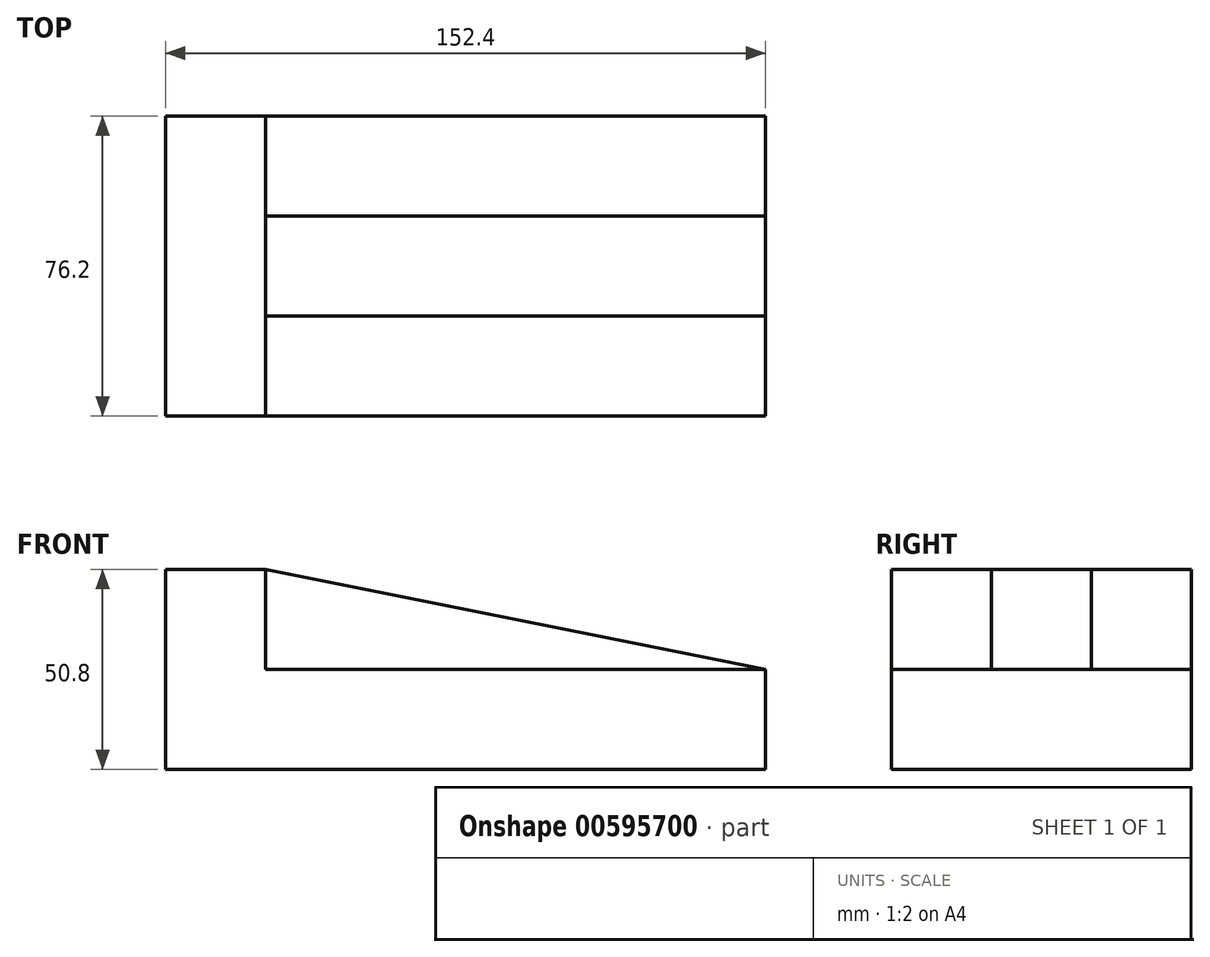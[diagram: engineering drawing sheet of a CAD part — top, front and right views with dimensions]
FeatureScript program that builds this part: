
annotation { "Feature Type Name" : "Feature", "Feature Type Description" : "" }
export const myFeature = defineFeature(function(context is Context, id is Id, definition is map)
    precondition{}
    {
        {
            var Q0;
            Q0=qCreatedBy(makeId("Top.planeOp"),FACE);
            var sketch = newSketch(context, id + "F0", { "sketchPlane" : qUnion([Q0])});
            skLineSegment(sketch, "E0", {"start": v(0, 0) * mm, "end": v(0, 76.2) * mm});
            skLineSegment(sketch, "E1", {"start": v(0, 76.2) * mm, "end": v(152.4, 76.2) * mm});
            skLineSegment(sketch, "E2", {"start": v(152.4, 76.2) * mm, "end": v(152.4, 0) * mm});
            skLineSegment(sketch, "E3", {"start": v(152.4, 0) * mm, "end": v(0, 0) * mm});
            skSolve(sketch);
        }
        {
            var Q0;
            Q0=makeQuery(id+"F0.imprint","IMPRINT",FACE,{"disambiguationData":[TD([[makeQuery(id+"F0.imprint","IMPRINT",EDGE,{"derivedFrom":sQuery(id+"F0.wireOp",EDGE,"E0")}),-1.0]])]});
            extrude(context, id + "F1", {"entities" : qUnion([Q0]), "depth" : 50.8 * mm, "offsetDistance" : 25.4 * mm});
        }
        {
            var Q0;
            Q0=makeQuery(id+"F1.opExtrude","SWEPT_FACE",FACE,{"disambiguationData":[OSD([sQuery(id+"F0.wireOp",EDGE,"E3")])]});
            var sketch = newSketch(context, id + "F2", { "sketchPlane" : qUnion([Q0])});
            skLineSegment(sketch, "E4", {"start": v(152.4, 25.4) * mm, "end": v(25.4, 25.4) * mm});
            skLineSegment(sketch, "E5", {"start": v(25.4, 25.4) * mm, "end": v(25.4, 50.8) * mm});
            skLineSegment(sketch, "E6", {"start": v(25.4, 50.8) * mm, "end": v(152.4, 50.8) * mm});
            skLineSegment(sketch, "E7", {"start": v(152.4, 50.8) * mm, "end": v(152.4, 25.4) * mm});
            skSolve(sketch);
        }
        {
            var Q0;
            Q0=makeQuery(id+"F2.imprint","IMPRINT",FACE,{"disambiguationData":[TD([[makeQuery(id+"F2.imprint","IMPRINT",EDGE,{"derivedFrom":sQuery(id+"F2.wireOp",EDGE,"E4")}),-1.0]])]});
            extrude(context, id + "F3", {"entities" : qUnion([Q0]), "operationType" : NewBodyOperationType.REMOVE, "oppositeDirection" : true, "depth" : 25.4 * mm, "offsetDistance" : 25.4 * mm});
        }
        {
            var Q0;
            Q0=makeQuery(id+"F1.opExtrude","SWEPT_FACE",FACE,{"disambiguationData":[OSD([sQuery(id+"F0.wireOp",EDGE,"E1")])]});
            var sketch = newSketch(context, id + "F4", { "sketchPlane" : qUnion([Q0])});
            skLineSegment(sketch, "E8.bottom", {"start": v(-152.4, 50.8) * mm, "end": v(-25.4, 50.8) * mm});
            skLineSegment(sketch, "E8.top", {"start": v(-152.4, 25.4) * mm, "end": v(-25.4, 25.4) * mm});
            skLineSegment(sketch, "E8.left", {"start": v(-152.4, 50.8) * mm, "end": v(-152.4, 25.4) * mm});
            skLineSegment(sketch, "E8.right", {"start": v(-25.4, 50.8) * mm, "end": v(-25.4, 25.4) * mm});
            skSolve(sketch);
        }
        {
            var Q0;
            Q0=makeQuery(id+"F4.imprint","IMPRINT",FACE,{"disambiguationData":[TD([[makeQuery(id+"F4.imprint","IMPRINT",EDGE,{"derivedFrom":sQuery(id+"F4.wireOp",EDGE,"E8.bottom")}),1.0]])]});
            extrude(context, id + "F5", {"entities" : qUnion([Q0]), "operationType" : NewBodyOperationType.REMOVE, "oppositeDirection" : true, "depth" : 25.4 * mm, "offsetDistance" : 25.4 * mm});
        }
        {
            var Q0;
            Q0=makeQuery(id+"F3.boolean.opBoolean","COPY",FACE,{"derivedFrom":makeQuery(id+"F3.opExtrude","CAP_FACE",FACE,{"disambiguationData":[OSD([sQuery(id+"F2.wireOp",EDGE,"E4"),sQuery(id+"F2.wireOp",EDGE,"E5"),sQuery(id+"F2.wireOp",EDGE,"E6"),sQuery(id+"F2.wireOp",EDGE,"E7")])],"isStart":false})});
            var sketch = newSketch(context, id + "F6", { "sketchPlane" : qUnion([Q0])});
            skLineSegment(sketch, "E9", {"start": v(25.4, 50.8) * mm, "end": v(152.4, 25.4) * mm});
            skLineSegment(sketch, "E10", {"start": v(152.4, 25.4) * mm, "end": v(152.4, 50.8) * mm});
            skLineSegment(sketch, "E11", {"start": v(152.4, 50.8) * mm, "end": v(25.4, 50.8) * mm});
            skSolve(sketch);
        }
        {
            var Q0;
            Q0=makeQuery(id+"F6.imprint","IMPRINT",FACE,{"disambiguationData":[TD([[makeQuery(id+"F6.imprint","IMPRINT",EDGE,{"derivedFrom":sQuery(id+"F6.wireOp",EDGE,"E9")}),1.0]])]});
            extrude(context, id + "F7", {"entities" : qUnion([Q0]), "operationType" : NewBodyOperationType.REMOVE, "oppositeDirection" : true, "depth" : 25.4 * mm, "offsetDistance" : 25.4 * mm});
        }
    });
